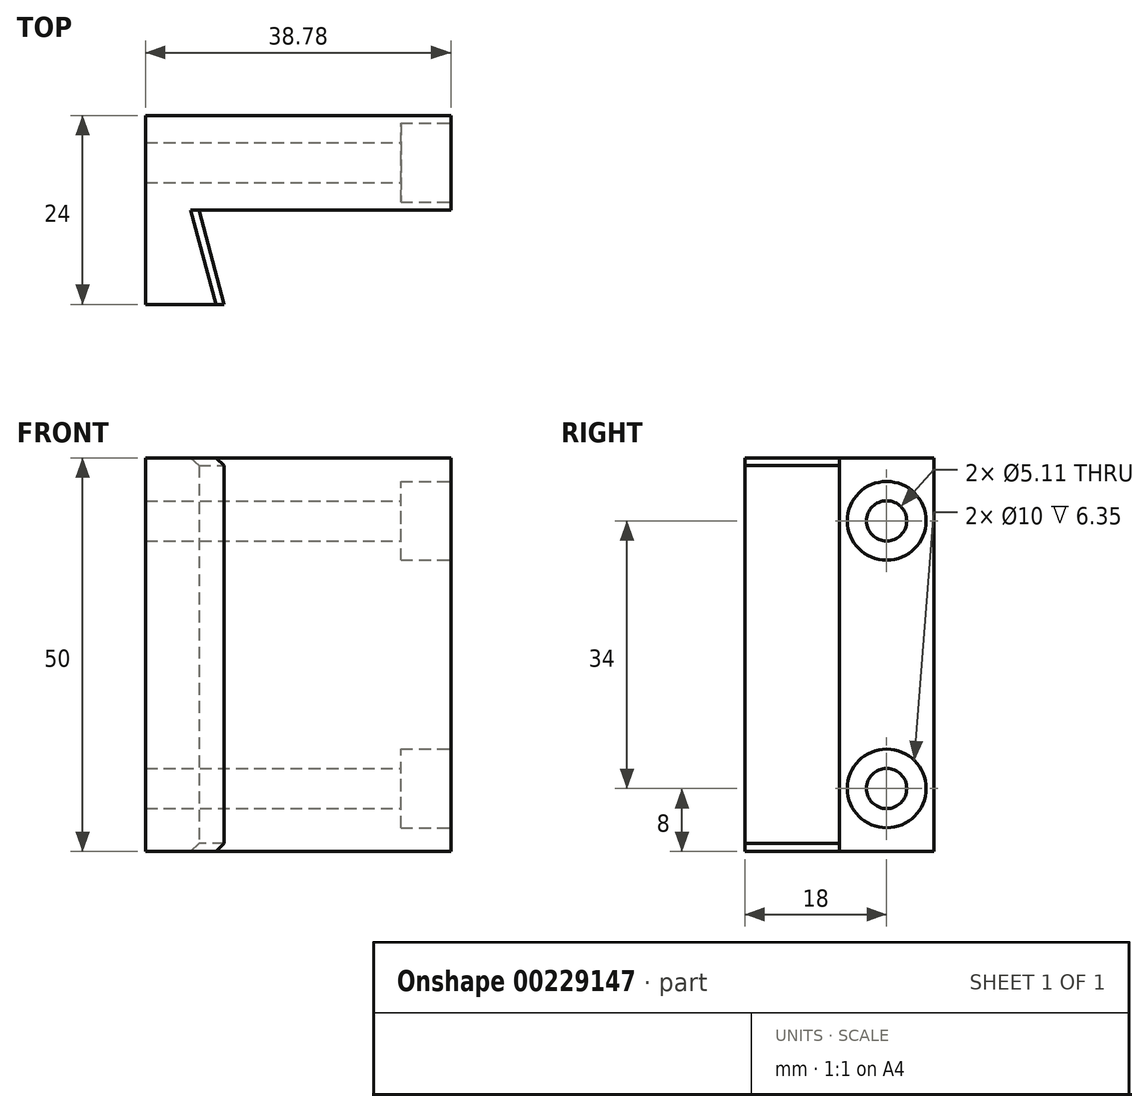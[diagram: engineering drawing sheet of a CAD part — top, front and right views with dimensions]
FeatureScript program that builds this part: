
annotation { "Feature Type Name" : "Feature", "Feature Type Description" : "" }
export const myFeature = defineFeature(function(context is Context, id is Id, definition is map)
    precondition{}
    {
        {
            var Q0;
            Q0=qCreatedBy(makeId("Top.planeOp"),FACE);
            var sketch = newSketch(context, id + "F0", { "sketchPlane" : qUnion([Q0])});
            skLineSegment(sketch, "E0", {"start": v(0, 0) * mm, "end": v(-32, 0) * mm});
            skLineSegment(sketch, "E1", {"start": v(-32, 0) * mm, "end": v(-28.78, -12) * mm});
            skLineSegment(sketch, "E2", {"start": v(-38.78, 12) * mm, "end": v(0, 12) * mm});
            skLineSegment(sketch, "E3", {"start": v(0, 12) * mm, "end": v(0, 0) * mm});
            skLineSegment(sketch, "E4", {"start": v(-38.78, 12) * mm, "end": v(-38.78, -12) * mm});
            skLineSegment(sketch, "E5", {"start": v(-38.78, -12) * mm, "end": v(-28.78, -12) * mm});
            skSolve(sketch);
        }
        {
            var Q0;
            Q0=qSketchRegion(id+"F0",true);
            extrude(context, id + "F1", {"entities" : qUnion([Q0]), "offsetDistance" : 25 * mm, "depth" : 50 * mm});
        }
        {
            var Q0;
            Q0=makeQuery(id+"F1.opExtrude","SWEPT_FACE",FACE,{"disambiguationData":[OSD([sQuery(id+"F0.wireOp",EDGE,"E3")])]});
            var sketch = newSketch(context, id + "F2", { "sketchPlane" : qUnion([Q0])});
            skLineSegment(sketch, "E6", {"start": v(6, 0) * mm, "end": v(6, 50) * mm, "construction": true});
            skLineSegment(sketch, "E7", {"start": v(12, 25) * mm, "end": v(0, 25) * mm, "construction": true});
            skPoint(sketch, "E8", {"position": v(6, 42) * mm});
            skPoint(sketch, "E9.MirrorP", {"position": v(6, 8) * mm});
            skSolve(sketch);
        }
        {
            var Q0;
            Q0=sQuery(id+"F2.wireOp",VERTEX,"E8");
            var Q1;
            Q1=sQuery(id+"F2.wireOp",VERTEX,"E9.MirrorP");
            var Q2;
            Q2=makeQuery(id+"F1.opExtrude","SWEPT_BODY",BODY,{"disambiguationData":[OSD([sQuery(id+"F0.wireOp",EDGE,"E0"),sQuery(id+"F0.wireOp",EDGE,"E1"),sQuery(id+"F0.wireOp",EDGE,"E2"),sQuery(id+"F0.wireOp",EDGE,"E3"),sQuery(id+"F0.wireOp",EDGE,"E4"),sQuery(id+"F0.wireOp",EDGE,"E5")])]});
            hole(context, id + "F3", {"style" : HoleStyle.C_BORE, "endStyle" : HoleEndStyle.THROUGH, "holeDiameter" : 5.1 * mm, "cBoreDiameter" : 10 * mm, "cBoreDepth" : 6.35 * mm, "majorDiameter" : 6.35 * mm, "isTappedThrough" : true, "tappedDepth" : 18 * mm, "tapClearance" : 3, "locations" : qUnion([Q0, Q1]), "scope" : qUnion([Q2])});
        }
        {
            var Q0;
            Q0=makeQuery(id+"F1.opExtrude","CAP_EDGE",EDGE,{"disambiguationData":[OSD([sQuery(id+"F0.wireOp",EDGE,"E1")])],"isStart":false});
            var Q1;
            Q1=makeQuery(id+"F1.opExtrude","CAP_EDGE",EDGE,{"disambiguationData":[OSD([sQuery(id+"F0.wireOp",EDGE,"E1")])],"isStart":true});
            chamfer(context, id + "F4", {"entities" : qUnion([Q0, Q1]), "width" : 1 * mm, "tangentPropagation" : true});
        }
    });
